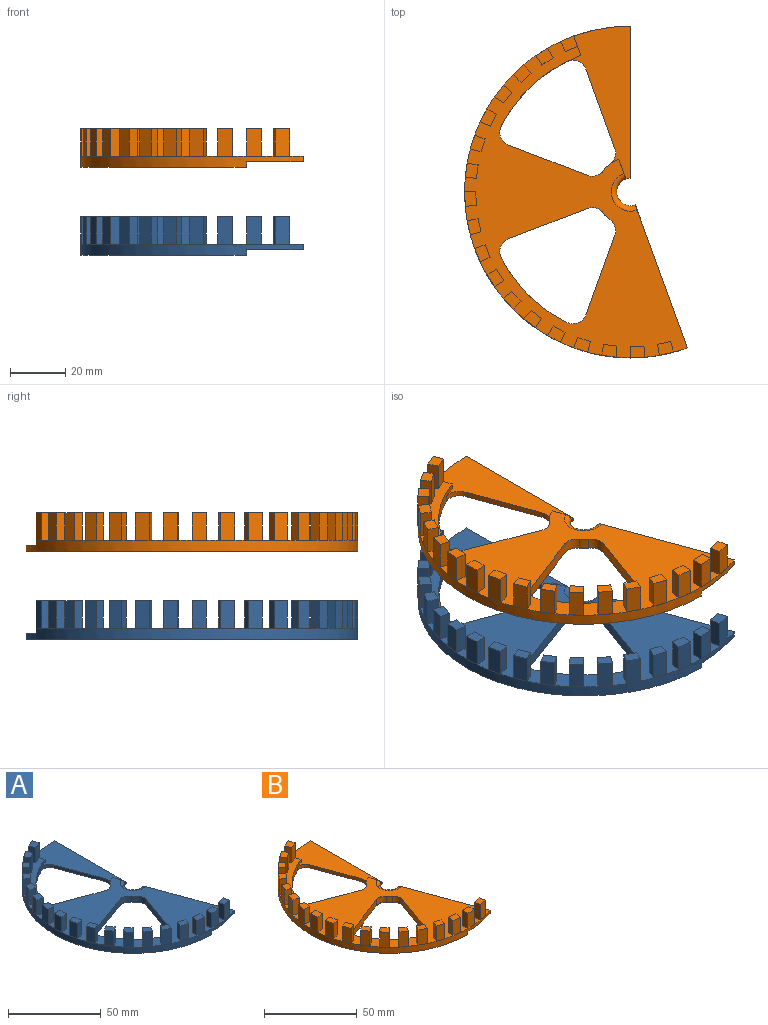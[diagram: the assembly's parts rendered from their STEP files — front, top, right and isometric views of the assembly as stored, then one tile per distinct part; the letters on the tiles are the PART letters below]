
ASSEMBLY  parts=2 mates=2
PART A: 139 faces, bbox 80.5x120x14 mm
  f0: plane 120x60mm, normal (0,0,-1), area 3247.2mm2, adj f22,f24,f26,f117,f118,f119,f120,f122
  f1: plane 114.38x80.52mm, normal (0,0,1), area 2971.4mm2, adj f2,f21,f23,f24,f28,f29,f33,f34
  f2: plane 12x7.05mm, normal (0.94,0.34,0), area 55mm2, adj f1,f24,f27,f29,f30,f31,f125
  f3: plane 5.11x1.13mm, normal (0,0,1), area 0.2mm2, adj f24,f112
  f4: plane 5.23x0.23mm, normal (0,0,1), area 0.2mm2, adj f24,f107
  f5: plane 5.19x0.68mm, normal (0,0,1), area 0.2mm2, adj f24,f102
  f6: plane 4.99x1.57mm, normal (0,0,1), area 0.2mm2, adj f24,f97
  f7: plane 4.64x2.42mm, normal (0,0,1), area 0.2mm2, adj f24,f92
  f8: plane 4.15x3.19mm, normal (0,0,1), area 0.2mm2, adj f24,f87
  f9: plane 3.86x3.54mm, normal (0,0,1), area 0.2mm2, adj f24,f82
  f10: plane 4.41x2.81mm, normal (0,0,1), area 0.2mm2, adj f24,f77
  f11: plane 4.84x2mm, normal (0,0,1), area 0.2mm2, adj f24,f72
  f12: plane 5.11x1.13mm, normal (0,0,1), area 0.2mm2, adj f24,f67
  f13: plane 5.23x0.23mm, normal (0,0,1), area 0.2mm2, adj f24,f62
  f14: plane 5.19x0.68mm, normal (0,0,1), area 0.2mm2, adj f24,f57
  f15: plane 4.99x1.57mm, normal (0,0,1), area 0.2mm2, adj f24,f52
  f16: plane 4.64x2.42mm, normal (0,0,1), area 0.2mm2, adj f24,f47
  f17: plane 4.15x3.19mm, normal (0,0,1), area 0.2mm2, adj f24,f42
  f18: plane 3.86x3.54mm, normal (0,0,1), area 0.2mm2, adj f24,f37
  f19: plane 4.41x2.81mm, normal (0,0,1), area 0.2mm2, adj f24,f32
  f20: plane 4.84x2mm, normal (0,0,1), area 0.2mm2, adj f24,f30
  f21: plane 7.05x2.57mm, normal (0.94,0.34,0), area 14.1mm2, adj f1,f27,f122,f123
  f22: plane 55x2mm, normal (1,0,0), area 109.1mm2, adj f0,f24,f27,f122
  f23: plane 51.68x18.81mm, normal (0.94,0.34,0), area 109.1mm2, adj f1,f24,f25,f122
  f24: cylinder r=60mm len=120mm, axis (0,0,-1), area 754mm2, adj f0,f1,f2,f3,f4,f5,f6,f7
  f25: plane 55.3x20.52mm, normal (0,0,-1), area 624mm2, adj f23,f24,f26,f122
  f26: plane 55x2mm, normal (1,0,0), area 109.1mm2, adj f0,f24,f25,f122
  f27: plane 55.3x23.05mm, normal (0,0,1), area 633.5mm2, adj f2,f21,f22,f24,f122,f123,f125,f126
  f28: plane 10x3.61mm, normal (-0.9,-0.43,0), area 40.1mm2, adj f1,f29,f30,f31
  f29: plane 10x4.47mm, normal (0.38,-0.92,0), area 48.4mm2, adj f1,f2,f28,f31
  f30: plane 10x4.84mm, normal (-0.38,0.92,0), area 52.3mm2, adj f2,f20,f28,f31
  f31: plane 6.21x5.62mm, normal (0,0,1), area 20.2mm2, adj f2,f28,f29,f30
  f32: plane 10x4.41mm, normal (-0.54,0.84,0), area 52.3mm2, adj f19,f33,f35,f36
  f33: plane 10x3.26mm, normal (-0.81,-0.58,0), area 40.1mm2, adj f1,f32,f34,f36
  f34: plane 10x4.08mm, normal (0.54,-0.84,0), area 48.4mm2, adj f1,f33,f35,f36
  f35: plane 10x3.47mm, normal (0.87,0.5,0), area 40mm2, adj f1,f32,f34,f36
  f36: plane 6.42x6.07mm, normal (0,0,1), area 20.2mm2, adj f32,f33,f34,f35
  f37: plane 10x3.86mm, normal (-0.68,0.74,0), area 52.3mm2, adj f18,f38,f40,f41
  f38: plane 10x2.86mm, normal (-0.7,-0.71,0), area 40.1mm2, adj f1,f37,f39,f41
  f39: plane 10x3.57mm, normal (0.68,-0.74,0), area 48.4mm2, adj f1,f38,f40,f41
  f40: plane 10x3.07mm, normal (0.77,0.64,0), area 40mm2, adj f1,f37,f39,f41
  f41: plane 6.43x6.34mm, normal (0,0,1), area 20.2mm2, adj f37,f38,f39,f40
  f42: plane 10x4.15mm, normal (-0.79,0.61,0), area 52.3mm2, adj f17,f43,f45,f46
  f43: plane 10x3.31mm, normal (-0.56,-0.83,0), area 40.1mm2, adj f1,f42,f44,f46
  f44: plane 10x3.84mm, normal (0.79,-0.61,0), area 48.4mm2, adj f1,f43,f45,f46
  f45: plane 10x3.07mm, normal (0.64,0.77,0), area 40mm2, adj f1,f42,f44,f46
  f46: plane 6.41x6.25mm, normal (0,0,1), area 20.2mm2, adj f42,f43,f44,f45
  f47: plane 10x4.64mm, normal (-0.89,0.46,0), area 52.3mm2, adj f16,f48,f50,f51
  f48: plane 10x3.65mm, normal (-0.41,-0.91,0), area 40.1mm2, adj f1,f47,f49,f51
  f49: plane 10x4.29mm, normal (0.89,-0.46,0), area 48.4mm2, adj f1,f48,f50,f51
  f50: plane 10x3.47mm, normal (0.5,0.87,0), area 40mm2, adj f1,f47,f49,f51
  f51: plane 6.3x5.88mm, normal (0,0,1), area 20.2mm2, adj f47,f48,f49,f50
  f52: plane 10x4.99mm, normal (-0.95,0.3,0), area 52.3mm2, adj f15,f53,f55,f56
  f53: plane 10x3.88mm, normal (-0.25,-0.97,0), area 40.1mm2, adj f1,f52,f54,f56
  f54: plane 10x4.62mm, normal (0.95,-0.3,0), area 48.4mm2, adj f1,f53,f55,f56
  f55: plane 10x3.76mm, normal (0.34,0.94,0), area 40mm2, adj f1,f52,f54,f56
  f56: plane 5.99x5.34mm, normal (0,0,1), area 20.2mm2, adj f52,f53,f54,f55
  f57: plane 10x5.19mm, normal (-0.99,0.13,0), area 52.3mm2, adj f14,f58,f60,f61
  f58: plane 10x3.99mm, normal (-0.08,-1,0), area 40.1mm2, adj f1,f57,f59,f61
  f59: plane 10x4.8mm, normal (0.99,-0.13,0), area 48.4mm2, adj f1,f58,f60,f61
  f60: plane 10x3.94mm, normal (0.17,0.98,0), area 40mm2, adj f1,f57,f59,f61
  f61: plane 5.5x4.63mm, normal (0,0,1), area 20.2mm2, adj f57,f58,f59,f60
  f62: plane 10x5.23mm, normal (-1,-0.04,0), area 52.3mm2, adj f13,f63,f65,f66
  f63: plane 10x3.99mm, normal (0.1,-1,0), area 40.1mm2, adj f1,f62,f64,f66
  f64: plane 10x4.84mm, normal (1,0.04,0), area 48.4mm2, adj f1,f63,f65,f66
  f65: plane 10x4mm, normal (0,1,0), area 40mm2, adj f1,f62,f64,f66
  f66: plane 5.23x4.22mm, normal (0,0,1), area 20.2mm2, adj f62,f63,f64,f65
  f67: plane 10x5.11mm, normal (-0.98,-0.22,0), area 52.3mm2, adj f12,f68,f70,f71
  f68: plane 10x3.86mm, normal (0.27,-0.96,0), area 40.1mm2, adj f1,f67,f69,f71
  f69: plane 10x4.73mm, normal (0.98,0.22,0), area 48.4mm2, adj f1,f68,f70,f71
  f70: plane 10x3.94mm, normal (-0.17,0.98,0), area 40mm2, adj f1,f67,f69,f71
  f71: plane 5.81x4.99mm, normal (0,0,1), area 20.2mm2, adj f67,f68,f69,f70
  f72: plane 10x4.84mm, normal (-0.92,-0.38,0), area 52.3mm2, adj f11,f73,f75,f76
  f73: plane 10x3.61mm, normal (0.43,-0.9,0), area 40.1mm2, adj f1,f72,f74,f76
  f74: plane 10x4.47mm, normal (0.92,0.38,0), area 48.4mm2, adj f1,f73,f75,f76
  f75: plane 10x3.76mm, normal (-0.34,0.94,0), area 40mm2, adj f1,f72,f74,f76
  f76: plane 6.21x5.62mm, normal (0,0,1), area 20.2mm2, adj f72,f73,f74,f75
  f77: plane 10x4.41mm, normal (-0.84,-0.54,0), area 52.3mm2, adj f10,f78,f80,f81
  f78: plane 10x3.26mm, normal (0.58,-0.81,0), area 40.1mm2, adj f1,f77,f79,f81
  f79: plane 10x4.08mm, normal (0.84,0.54,0), area 48.4mm2, adj f1,f78,f80,f81
  f80: plane 10x3.47mm, normal (-0.5,0.87,0), area 40mm2, adj f1,f77,f79,f81
  f81: plane 6.42x6.07mm, normal (0,0,1), area 20.2mm2, adj f77,f78,f79,f80
  f82: plane 10x3.86mm, normal (-0.74,-0.68,0), area 52.3mm2, adj f9,f83,f85,f86
  f83: plane 10x2.86mm, normal (0.71,-0.7,0), area 40.1mm2, adj f1,f82,f84,f86
  f84: plane 10x3.57mm, normal (0.74,0.68,0), area 48.4mm2, adj f1,f83,f85,f86
  f85: plane 10x3.07mm, normal (-0.64,0.77,0), area 40mm2, adj f1,f82,f84,f86
  f86: plane 6.43x6.34mm, normal (0,0,1), area 20.2mm2, adj f82,f83,f84,f85
  f87: plane 10x4.15mm, normal (-0.61,-0.79,0), area 52.3mm2, adj f8,f88,f90,f91
  f88: plane 10x3.31mm, normal (0.83,-0.56,0), area 40.1mm2, adj f1,f87,f89,f91
  f89: plane 10x3.84mm, normal (0.61,0.79,0), area 48.4mm2, adj f1,f88,f90,f91
  f90: plane 10x3.07mm, normal (-0.77,0.64,0), area 40mm2, adj f1,f87,f89,f91
  f91: plane 6.41x6.25mm, normal (0,0,1), area 20.2mm2, adj f87,f88,f89,f90
  f92: plane 10x4.64mm, normal (-0.46,-0.89,0), area 52.3mm2, adj f7,f93,f95,f96
  f93: plane 10x3.65mm, normal (0.91,-0.41,0), area 40.1mm2, adj f1,f92,f94,f96
  f94: plane 10x4.29mm, normal (0.46,0.89,0), area 48.4mm2, adj f1,f93,f95,f96
  f95: plane 10x3.47mm, normal (-0.87,0.5,0), area 40mm2, adj f1,f92,f94,f96
  f96: plane 6.3x5.88mm, normal (0,0,1), area 20.2mm2, adj f92,f93,f94,f95
  f97: plane 10x4.99mm, normal (-0.3,-0.95,0), area 52.3mm2, adj f6,f98,f100,f101
  f98: plane 10x3.88mm, normal (0.97,-0.25,0), area 40.1mm2, adj f1,f97,f99,f101
  f99: plane 10x4.62mm, normal (0.3,0.95,0), area 48.4mm2, adj f1,f98,f100,f101
  f100: plane 10x3.76mm, normal (-0.94,0.34,0), area 40mm2, adj f1,f97,f99,f101
  f101: plane 5.99x5.34mm, normal (0,0,1), area 20.2mm2, adj f97,f98,f99,f100
  f102: plane 10x5.19mm, normal (-0.13,-0.99,0), area 52.3mm2, adj f5,f103,f105,f106
  f103: plane 10x3.99mm, normal (1,-0.08,0), area 40.1mm2, adj f1,f102,f104,f106
  f104: plane 10x4.8mm, normal (0.13,0.99,0), area 48.4mm2, adj f1,f103,f105,f106
  f105: plane 10x3.94mm, normal (-0.98,0.17,0), area 40mm2, adj f1,f102,f104,f106
  f106: plane 5.5x4.63mm, normal (0,0,1), area 20.2mm2, adj f102,f103,f104,f105
  f107: plane 10x5.23mm, normal (0.04,-1,0), area 52.3mm2, adj f4,f108,f110,f111
  f108: plane 10x3.99mm, normal (1,0.1,0), area 40.1mm2, adj f1,f107,f109,f111
  f109: plane 10x4.84mm, normal (-0.04,1,0), area 48.4mm2, adj f1,f108,f110,f111
  f110: plane 10x4mm, normal (-1,0,0), area 40mm2, adj f1,f107,f109,f111
  f111: plane 5.23x4.22mm, normal (0,0,1), area 20.2mm2, adj f107,f108,f109,f110
  f112: plane 10x5.11mm, normal (0.22,-0.98,0), area 52.3mm2, adj f3,f113,f115,f116
  f113: plane 10x3.86mm, normal (0.96,0.27,0), area 40.1mm2, adj f1,f112,f114,f116
  f114: plane 10x4.73mm, normal (-0.22,0.98,0), area 48.4mm2, adj f1,f113,f115,f116
  f115: plane 10x3.94mm, normal (-0.98,-0.17,0), area 40mm2, adj f1,f112,f114,f116
  f116: plane 5.81x4.99mm, normal (0,0,1), area 20.2mm2, adj f112,f113,f114,f115
  f117: plane 20x1mm, normal (-1,0,0), area 20mm2, adj f0,f118,f120,f121
  f118: plane 5x1mm, normal (0,1,0), area 5mm2, adj f0,f117,f119,f121
  f119: plane 20x1mm, normal (1,0,0), area 20mm2, adj f0,f118,f120,f121
  f120: plane 5x1mm, normal (0,-1,0), area 5mm2, adj f0,f117,f119,f121
  f121: plane 20x5mm, normal (0,0,-1), area 100mm2, adj f117,f118,f119,f120
  f122: torus R=7mm, axis (0,0,1), area 113mm2, adj f0,f1,f21,f22,f23,f25,f26,f27
  f123: cylinder r=12.5mm len=5.76mm, axis (0,0,-1), area 21.9mm2, adj f0,f1,f21,f27,f131,f133
  f124: plane 28.63x10.42mm, normal (0.34,0.94,0), area 121.9mm2, adj f0,f1,f133,f134
  f125: cylinder r=52.5mm len=29.21mm, axis (0,0,-1), area 150mm2, adj f0,f1,f2,f27,f132,f134
  f126: plane 28.63x10.42mm, normal (-0.94,-0.34,0), area 60.9mm2, adj f0,f27,f131,f132
  f127: cylinder r=12.5mm len=4mm, axis (0,0,-1), area 14.7mm2, adj f0,f1,f135,f138
  f128: plane 28.63x10.42mm, normal (-0.94,0.34,0), area 121.9mm2, adj f0,f1,f137,f138
  f129: cylinder r=52.5mm len=24.12mm, axis (0,0,-1), area 139mm2, adj f0,f1,f136,f137
  f130: plane 28.63x10.42mm, normal (0.34,-0.94,0), area 121.9mm2, adj f0,f1,f135,f136
  f131: cylinder r=5mm len=5.72mm, axis (0,0,-1), area 12.8mm2, adj f0,f27,f123,f126
  f132: cylinder r=5mm len=6.89mm, axis (0,0,-1), area 16.8mm2, adj f0,f27,f125,f126
  f133: cylinder r=5mm len=5.72mm, axis (0,0,-1), area 25.6mm2, adj f0,f1,f123,f124
  f134: cylinder r=5mm len=6.89mm, axis (0,0,-1), area 33.5mm2, adj f0,f1,f124,f125
  f135: cylinder r=5mm len=5.72mm, axis (0,0,-1), area 25.6mm2, adj f0,f1,f127,f130
  f136: cylinder r=5mm len=6.89mm, axis (0,0,-1), area 33.5mm2, adj f0,f1,f129,f130
  f137: cylinder r=5mm len=6.89mm, axis (0,0,-1), area 33.5mm2, adj f0,f1,f128,f129
  f138: cylinder r=5mm len=5.72mm, axis (0,0,-1), area 25.6mm2, adj f0,f1,f127,f128
PART B: 139 faces, bbox 80.5x120x14 mm
  f0: plane 120x60mm, normal (0,0,-1), area 3291.3mm2, adj f22,f24,f26,f117,f118,f119,f120,f122
  f1: plane 114.38x80.52mm, normal (0,0,1), area 3016.7mm2, adj f2,f21,f23,f24,f28,f29,f33,f34
  f2: plane 12x7.05mm, normal (0.94,0.34,0), area 55mm2, adj f1,f24,f27,f29,f30,f31,f129
  f3: plane 5.11x1.13mm, normal (0,0,1), area 0.2mm2, adj f24,f112
  f4: plane 5.23x0.23mm, normal (0,0,1), area 0.2mm2, adj f24,f107
  f5: plane 5.19x0.68mm, normal (0,0,1), area 0.2mm2, adj f24,f102
  f6: plane 4.99x1.57mm, normal (0,0,1), area 0.2mm2, adj f24,f97
  f7: plane 4.64x2.42mm, normal (0,0,1), area 0.2mm2, adj f24,f92
  f8: plane 4.15x3.19mm, normal (0,0,1), area 0.2mm2, adj f24,f87
  f9: plane 3.86x3.54mm, normal (0,0,1), area 0.2mm2, adj f24,f82
  f10: plane 4.41x2.81mm, normal (0,0,1), area 0.2mm2, adj f24,f77
  f11: plane 4.84x2mm, normal (0,0,1), area 0.2mm2, adj f24,f72
  f12: plane 5.11x1.13mm, normal (0,0,1), area 0.2mm2, adj f24,f67
  f13: plane 5.23x0.23mm, normal (0,0,1), area 0.2mm2, adj f24,f62
  f14: plane 5.19x0.68mm, normal (0,0,1), area 0.2mm2, adj f24,f57
  f15: plane 4.99x1.57mm, normal (0,0,1), area 0.2mm2, adj f24,f52
  f16: plane 4.64x2.42mm, normal (0,0,1), area 0.2mm2, adj f24,f47
  f17: plane 4.15x3.19mm, normal (0,0,1), area 0.2mm2, adj f24,f42
  f18: plane 3.86x3.54mm, normal (0,0,1), area 0.2mm2, adj f24,f37
  f19: plane 4.41x2.81mm, normal (0,0,1), area 0.2mm2, adj f24,f32
  f20: plane 4.84x2mm, normal (0,0,1), area 0.2mm2, adj f24,f30
  f21: plane 7.05x2.57mm, normal (0.94,0.34,0), area 14.1mm2, adj f1,f27,f122,f127
  f22: plane 55x2mm, normal (1,0,0), area 109.1mm2, adj f0,f24,f27,f122
  f23: plane 51.68x18.81mm, normal (0.94,0.34,0), area 109.1mm2, adj f1,f24,f25,f122
  f24: cylinder r=60mm len=120mm, axis (0,0,-1), area 754mm2, adj f0,f1,f2,f3,f4,f5,f6,f7
  f25: plane 55.3x20.52mm, normal (0,0,-1), area 624mm2, adj f23,f24,f26,f122
  f26: plane 55x2mm, normal (1,0,0), area 109.1mm2, adj f0,f24,f25,f122
  f27: plane 55.3x23.05mm, normal (0,0,1), area 633.5mm2, adj f2,f21,f22,f24,f122,f127,f129,f130
  f28: plane 10x3.61mm, normal (-0.9,-0.43,0), area 40.1mm2, adj f1,f29,f30,f31
  f29: plane 10x4.47mm, normal (0.38,-0.92,0), area 48.4mm2, adj f1,f2,f28,f31
  f30: plane 10x4.84mm, normal (-0.38,0.92,0), area 52.3mm2, adj f2,f20,f28,f31
  f31: plane 6.21x5.62mm, normal (0,0,1), area 20.2mm2, adj f2,f28,f29,f30
  f32: plane 10x4.41mm, normal (-0.54,0.84,0), area 52.3mm2, adj f19,f33,f35,f36
  f33: plane 10x3.26mm, normal (-0.81,-0.58,0), area 40.1mm2, adj f1,f32,f34,f36
  f34: plane 10x4.08mm, normal (0.54,-0.84,0), area 48.4mm2, adj f1,f33,f35,f36
  f35: plane 10x3.47mm, normal (0.87,0.5,0), area 40mm2, adj f1,f32,f34,f36
  f36: plane 6.42x6.07mm, normal (0,0,1), area 20.2mm2, adj f32,f33,f34,f35
  f37: plane 10x3.86mm, normal (-0.68,0.74,0), area 52.3mm2, adj f18,f38,f40,f41
  f38: plane 10x2.86mm, normal (-0.7,-0.71,0), area 40.1mm2, adj f1,f37,f39,f41
  f39: plane 10x3.57mm, normal (0.68,-0.74,0), area 48.4mm2, adj f1,f38,f40,f41
  f40: plane 10x3.07mm, normal (0.77,0.64,0), area 40mm2, adj f1,f37,f39,f41
  f41: plane 6.43x6.34mm, normal (0,0,1), area 20.2mm2, adj f37,f38,f39,f40
  f42: plane 10x4.15mm, normal (-0.79,0.61,0), area 52.3mm2, adj f17,f43,f45,f46
  f43: plane 10x3.31mm, normal (-0.56,-0.83,0), area 40.1mm2, adj f1,f42,f44,f46
  f44: plane 10x3.84mm, normal (0.79,-0.61,0), area 48.4mm2, adj f1,f43,f45,f46
  f45: plane 10x3.07mm, normal (0.64,0.77,0), area 40mm2, adj f1,f42,f44,f46
  f46: plane 6.41x6.25mm, normal (0,0,1), area 20.2mm2, adj f42,f43,f44,f45
  f47: plane 10x4.64mm, normal (-0.89,0.46,0), area 52.3mm2, adj f16,f48,f50,f51
  f48: plane 10x3.65mm, normal (-0.41,-0.91,0), area 40.1mm2, adj f1,f47,f49,f51
  f49: plane 10x4.29mm, normal (0.89,-0.46,0), area 48.4mm2, adj f1,f48,f50,f51
  f50: plane 10x3.47mm, normal (0.5,0.87,0), area 40mm2, adj f1,f47,f49,f51
  f51: plane 6.3x5.88mm, normal (0,0,1), area 20.2mm2, adj f47,f48,f49,f50
  f52: plane 10x4.99mm, normal (-0.95,0.3,0), area 52.3mm2, adj f15,f53,f55,f56
  f53: plane 10x3.88mm, normal (-0.25,-0.97,0), area 40.1mm2, adj f1,f52,f54,f56
  f54: plane 10x4.62mm, normal (0.95,-0.3,0), area 48.4mm2, adj f1,f53,f55,f56
  f55: plane 10x3.76mm, normal (0.34,0.94,0), area 40mm2, adj f1,f52,f54,f56
  f56: plane 5.99x5.34mm, normal (0,0,1), area 20.2mm2, adj f52,f53,f54,f55
  f57: plane 10x5.19mm, normal (-0.99,0.13,0), area 52.3mm2, adj f14,f58,f60,f61
  f58: plane 10x3.99mm, normal (-0.08,-1,0), area 40.1mm2, adj f1,f57,f59,f61
  f59: plane 10x4.8mm, normal (0.99,-0.13,0), area 48.4mm2, adj f1,f58,f60,f61
  f60: plane 10x3.94mm, normal (0.17,0.98,0), area 40mm2, adj f1,f57,f59,f61
  f61: plane 5.5x4.63mm, normal (0,0,1), area 20.2mm2, adj f57,f58,f59,f60
  f62: plane 10x5.23mm, normal (-1,-0.04,0), area 52.3mm2, adj f13,f63,f65,f66
  f63: plane 10x3.99mm, normal (0.1,-1,0), area 40.1mm2, adj f1,f62,f64,f66
  f64: plane 10x4.84mm, normal (1,0.04,0), area 48.4mm2, adj f1,f63,f65,f66
  f65: plane 10x4mm, normal (0,1,0), area 40mm2, adj f1,f62,f64,f66
  f66: plane 5.23x4.22mm, normal (0,0,1), area 20.2mm2, adj f62,f63,f64,f65
  f67: plane 10x5.11mm, normal (-0.98,-0.22,0), area 52.3mm2, adj f12,f68,f70,f71
  f68: plane 10x3.86mm, normal (0.27,-0.96,0), area 40.1mm2, adj f1,f67,f69,f71
  f69: plane 10x4.73mm, normal (0.98,0.22,0), area 48.4mm2, adj f1,f68,f70,f71
  f70: plane 10x3.94mm, normal (-0.17,0.98,0), area 40mm2, adj f1,f67,f69,f71
  f71: plane 5.81x4.99mm, normal (0,0,1), area 20.2mm2, adj f67,f68,f69,f70
  f72: plane 10x4.84mm, normal (-0.92,-0.38,0), area 52.3mm2, adj f11,f73,f75,f76
  f73: plane 10x3.61mm, normal (0.43,-0.9,0), area 40.1mm2, adj f1,f72,f74,f76
  f74: plane 10x4.47mm, normal (0.92,0.38,0), area 48.4mm2, adj f1,f73,f75,f76
  f75: plane 10x3.76mm, normal (-0.34,0.94,0), area 40mm2, adj f1,f72,f74,f76
  f76: plane 6.21x5.62mm, normal (0,0,1), area 20.2mm2, adj f72,f73,f74,f75
  f77: plane 10x4.41mm, normal (-0.84,-0.54,0), area 52.3mm2, adj f10,f78,f80,f81
  f78: plane 10x3.26mm, normal (0.58,-0.81,0), area 40.1mm2, adj f1,f77,f79,f81
  f79: plane 10x4.08mm, normal (0.84,0.54,0), area 48.4mm2, adj f1,f78,f80,f81
  f80: plane 10x3.47mm, normal (-0.5,0.87,0), area 40mm2, adj f1,f77,f79,f81
  f81: plane 6.42x6.07mm, normal (0,0,1), area 20.2mm2, adj f77,f78,f79,f80
  f82: plane 10x3.86mm, normal (-0.74,-0.68,0), area 52.3mm2, adj f9,f83,f85,f86
  f83: plane 10x2.86mm, normal (0.71,-0.7,0), area 40.1mm2, adj f1,f82,f84,f86
  f84: plane 10x3.57mm, normal (0.74,0.68,0), area 48.4mm2, adj f1,f83,f85,f86
  f85: plane 10x3.07mm, normal (-0.64,0.77,0), area 40mm2, adj f1,f82,f84,f86
  f86: plane 6.43x6.34mm, normal (0,0,1), area 20.2mm2, adj f82,f83,f84,f85
  f87: plane 10x4.15mm, normal (-0.61,-0.79,0), area 52.3mm2, adj f8,f88,f90,f91
  f88: plane 10x3.31mm, normal (0.83,-0.56,0), area 40.1mm2, adj f1,f87,f89,f91
  f89: plane 10x3.84mm, normal (0.61,0.79,0), area 48.4mm2, adj f1,f88,f90,f91
  f90: plane 10x3.07mm, normal (-0.77,0.64,0), area 40mm2, adj f1,f87,f89,f91
  f91: plane 6.41x6.25mm, normal (0,0,1), area 20.2mm2, adj f87,f88,f89,f90
  f92: plane 10x4.64mm, normal (-0.46,-0.89,0), area 52.3mm2, adj f7,f93,f95,f96
  f93: plane 10x3.65mm, normal (0.91,-0.41,0), area 40.1mm2, adj f1,f92,f94,f96
  f94: plane 10x4.29mm, normal (0.46,0.89,0), area 48.4mm2, adj f1,f93,f95,f96
  f95: plane 10x3.47mm, normal (-0.87,0.5,0), area 40mm2, adj f1,f92,f94,f96
  f96: plane 6.3x5.88mm, normal (0,0,1), area 20.2mm2, adj f92,f93,f94,f95
  f97: plane 10x4.99mm, normal (-0.3,-0.95,0), area 52.3mm2, adj f6,f98,f100,f101
  f98: plane 10x3.88mm, normal (0.97,-0.25,0), area 40.1mm2, adj f1,f97,f99,f101
  f99: plane 10x4.62mm, normal (0.3,0.95,0), area 48.4mm2, adj f1,f98,f100,f101
  f100: plane 10x3.76mm, normal (-0.94,0.34,0), area 40mm2, adj f1,f97,f99,f101
  f101: plane 5.99x5.34mm, normal (0,0,1), area 20.2mm2, adj f97,f98,f99,f100
  f102: plane 10x5.19mm, normal (-0.13,-0.99,0), area 52.3mm2, adj f5,f103,f105,f106
  f103: plane 10x3.99mm, normal (1,-0.08,0), area 40.1mm2, adj f1,f102,f104,f106
  f104: plane 10x4.8mm, normal (0.13,0.99,0), area 48.4mm2, adj f1,f103,f105,f106
  f105: plane 10x3.94mm, normal (-0.98,0.17,0), area 40mm2, adj f1,f102,f104,f106
  f106: plane 5.5x4.63mm, normal (0,0,1), area 20.2mm2, adj f102,f103,f104,f105
  f107: plane 10x5.23mm, normal (0.04,-1,0), area 52.3mm2, adj f4,f108,f110,f111
  f108: plane 10x3.99mm, normal (1,0.1,0), area 40.1mm2, adj f1,f107,f109,f111
  f109: plane 10x4.84mm, normal (-0.04,1,0), area 48.4mm2, adj f1,f108,f110,f111
  f110: plane 10x4mm, normal (-1,0,0), area 40mm2, adj f1,f107,f109,f111
  f111: plane 5.23x4.22mm, normal (0,0,1), area 20.2mm2, adj f107,f108,f109,f110
  f112: plane 10x5.11mm, normal (0.22,-0.98,0), area 52.3mm2, adj f3,f113,f115,f116
  f113: plane 10x3.86mm, normal (0.96,0.27,0), area 40.1mm2, adj f1,f112,f114,f116
  f114: plane 10x4.73mm, normal (-0.22,0.98,0), area 48.4mm2, adj f1,f113,f115,f116
  f115: plane 10x3.94mm, normal (-0.98,-0.17,0), area 40mm2, adj f1,f112,f114,f116
  f116: plane 5.81x4.99mm, normal (0,0,1), area 20.2mm2, adj f112,f113,f114,f115
  f117: cylinder r=30mm len=20mm, axis (0,0,-1), area 20.4mm2, adj f0,f118,f120,f121
  f118: plane 6.22x1mm, normal (0,1,0), area 6.2mm2, adj f0,f117,f119,f121
  f119: plane 20x1mm, normal (1,0,0), area 20mm2, adj f0,f118,f120,f121
  f120: plane 6.22x1mm, normal (0,-1,0), area 6.2mm2, adj f0,f117,f119,f121
  f121: plane 20x6.22mm, normal (0,0,-1), area 101.3mm2, adj f117,f118,f119,f120
  f122: torus R=7mm, axis (0,0,1), area 113mm2, adj f0,f1,f21,f22,f23,f25,f26,f27
  f123: cylinder r=12.5mm len=4mm, axis (0,0,-1), area 13.8mm2, adj f0,f1,f133,f136
  f124: plane 28.63x10.42mm, normal (-0.94,0.34,0), area 121.9mm2, adj f0,f1,f133,f134
  f125: cylinder r=52.5mm len=23.71mm, axis (0,0,-1), area 135.3mm2, adj f0,f1,f134,f135
  f126: plane 28.44x10.92mm, normal (0.36,-0.93,0), area 121.9mm2, adj f0,f1,f135,f136
  f127: cylinder r=12.5mm len=5.63mm, axis (0,0,-1), area 21mm2, adj f0,f1,f21,f27,f131,f138
  f128: plane 28.44x10.92mm, normal (0.36,0.93,0), area 121.9mm2, adj f0,f1,f137,f138
  f129: cylinder r=52.5mm len=28.8mm, axis (0,0,-1), area 146.4mm2, adj f0,f1,f2,f27,f132,f137
  f130: plane 28.63x10.42mm, normal (-0.94,-0.34,0), area 60.9mm2, adj f0,f27,f131,f132
  f131: cylinder r=5mm len=5.72mm, axis (0,0,-1), area 12.8mm2, adj f0,f27,f127,f130
  f132: cylinder r=5mm len=6.89mm, axis (0,0,-1), area 16.8mm2, adj f0,f27,f129,f130
  f133: cylinder r=5mm len=5.72mm, axis (0,0,-1), area 25.6mm2, adj f0,f1,f123,f124
  f134: cylinder r=5mm len=6.89mm, axis (0,0,-1), area 33.5mm2, adj f0,f1,f124,f125
  f135: cylinder r=5mm len=6.94mm, axis (0,0,-1), area 33.5mm2, adj f0,f1,f125,f126
  f136: cylinder r=5mm len=5.75mm, axis (0,0,-1), area 25.6mm2, adj f0,f1,f123,f126
  f137: cylinder r=5mm len=6.94mm, axis (0,0,-1), area 33.5mm2, adj f0,f1,f128,f129
  f138: cylinder r=5mm len=5.75mm, axis (0,0,-1), area 25.6mm2, adj f0,f1,f127,f128
PLACE A t=(-97.03,-58.61,9.76)mm
PLACE B t=(-97.03,-58.61,41.55)mm
MATE planar A.f22 <-> B.f26  axis (1,0,0) through (-97.03,-25.9,8.77)mm
MATE planar A.f23 <-> B.f2  axis (0.94,0.34,0) through (-85.84,-89.35,10.76)mm
